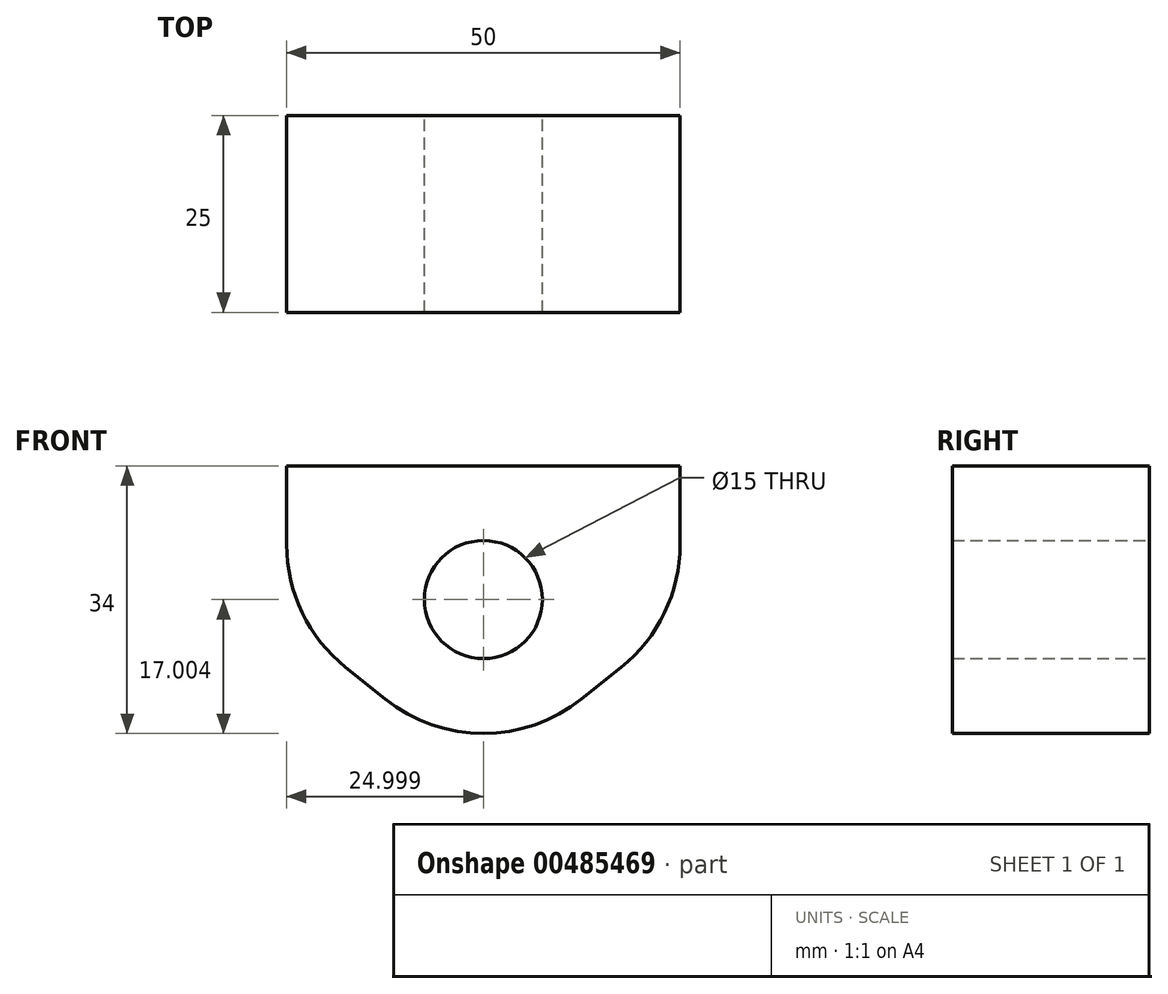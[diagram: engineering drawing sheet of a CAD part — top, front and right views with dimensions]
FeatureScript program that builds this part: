
annotation { "Feature Type Name" : "Feature", "Feature Type Description" : "" }
export const myFeature = defineFeature(function(context is Context, id is Id, definition is map)
    precondition{}
    {
        {
            var Q0;
            Q0=qCreatedBy(makeId("Front.planeOp"),FACE);
            var sketch = newSketch(context, id + "F0", { "sketchPlane" : qUnion([Q0])});
            skLineSegment(sketch, "E0", {"start": v(-32.26, 16.36) * mm, "end": v(17.74, 16.36) * mm});
            skLineSegment(sketch, "E1", {"start": v(-32.26, 16.36) * mm, "end": v(-32.26, 6.36) * mm});
            skLineSegment(sketch, "E2", {"start": v(17.74, 16.36) * mm, "end": v(17.74, 6.36) * mm});
            skPoint(sketch, "E3", {"position": v(-7.26, -0.64) * mm});
            skCircle(sketch, "E4", {"center": v(-7.26, -0.64) * mm, "radius": 7.5 * mm});
            skLineSegment(sketch, "E5", {"start": v(-24.75, -9.25) * mm, "end": v(-19.75, -13.25) * mm});
            skLineSegment(sketch, "E6", {"start": v(5.23, -13.25) * mm, "end": v(10.23, -9.25) * mm});
            skArc(sketch, "E7.filletArc", {"start": v(-32.26, 6.36) * mm, "mid": v(-30.29, -2.3) * mm, "end": v(-24.75, -9.25) * mm});
            skPoint(sketch, "E8.visualSharp", {"position": v(-7.26, -23.25) * mm});
            skArc(sketch, "E8.filletArc", {"start": v(-19.75, -13.25) * mm, "mid": v(-7.26, -17.64) * mm, "end": v(5.23, -13.25) * mm});
            skArc(sketch, "E9.filletArc", {"start": v(10.23, -9.25) * mm, "mid": v(15.77, -2.3) * mm, "end": v(17.74, 6.36) * mm});
            skSolve(sketch);
        }
        {
            var Q0;
            Q0=makeQuery(id+"F0.imprint","IMPRINT",FACE,{"disambiguationData":[TD([[makeQuery(id+"F0.imprint","IMPRINT",EDGE,{"derivedFrom":sQuery(id+"F0.wireOp",EDGE,"E0")}),-1.0]])]});
            extrude(context, id + "F1", {"entities" : qUnion([Q0]), "depth" : 25 * mm});
        }
    });
